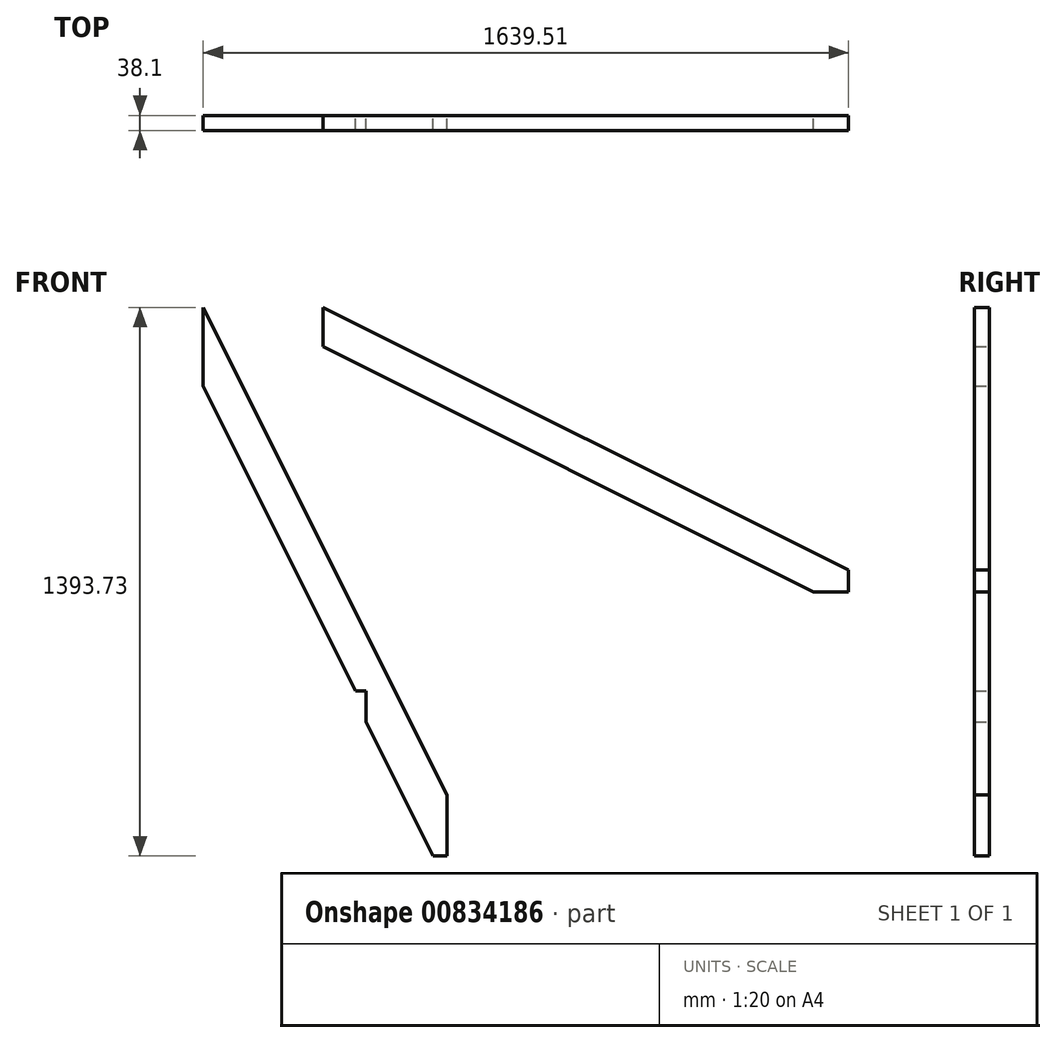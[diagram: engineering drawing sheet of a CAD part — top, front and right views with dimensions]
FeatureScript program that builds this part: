
annotation { "Feature Type Name" : "Feature", "Feature Type Description" : "" }
export const myFeature = defineFeature(function(context is Context, id is Id, definition is map)
    precondition{}
    {
        {
            var Q0;
            Q0=qCreatedBy(makeId("Front.planeOp"),FACE);
            var sketch = newSketch(context, id + "F0", { "sketchPlane" : qUnion([Q0])});
            skLineSegment(sketch, "E0", {"start": v(0, 0) * mm, "end": v(304.8, 0) * mm, "construction": true});
            skLineSegment(sketch, "E1", {"start": v(304.8, 0) * mm, "end": v(304.8, -609.6) * mm, "construction": true});
            skLineSegment(sketch, "E2", {"start": v(304.8, -609.6) * mm, "end": v(0, 0) * mm, "construction": true});
            skLineSegment(sketch, "E3", {"start": v(304.8, -609.6) * mm, "end": v(225.29, -649.36) * mm, "construction": true});
            skLineSegment(sketch, "E4", {"start": v(0, 0) * mm, "end": v(619.08, -1238.16) * mm});
            skLineSegment(sketch, "E5", {"start": v(619.08, -1238.16) * mm, "end": v(619.08, -1393.73) * mm});
            skLineSegment(sketch, "E6", {"start": v(619.08, -1393.73) * mm, "end": v(584.15, -1393.73) * mm});
            skLineSegment(sketch, "E7", {"start": v(584.15, -1393.73) * mm, "end": v(413.76, -1052.95) * mm});
            skLineSegment(sketch, "E8", {"start": v(413.76, -1052.95) * mm, "end": v(413.76, -973.58) * mm});
            skLineSegment(sketch, "E9", {"start": v(413.76, -973.58) * mm, "end": v(387.4, -973.58) * mm});
            skLineSegment(sketch, "E10", {"start": v(387.4, -973.58) * mm, "end": v(0, -198.79) * mm});
            skLineSegment(sketch, "E11", {"start": v(0, -198.79) * mm, "end": v(0, 0) * mm});
            skLineSegment(sketch, "E12", {"start": v(304.8, 0) * mm, "end": v(609.6, 0) * mm, "construction": true});
            skLineSegment(sketch, "E13", {"start": v(609.6, 0) * mm, "end": v(609.6, -152.4) * mm, "construction": true});
            skLineSegment(sketch, "E14", {"start": v(609.6, -152.4) * mm, "end": v(304.8, 0) * mm, "construction": true});
            skLineSegment(sketch, "E15", {"start": v(304.8, 0) * mm, "end": v(1639.5, -667.35) * mm});
            skLineSegment(sketch, "E16", {"start": v(1639.5, -667.35) * mm, "end": v(1639.5, -722.3) * mm});
            skLineSegment(sketch, "E17", {"start": v(1639.5, -722.3) * mm, "end": v(1550.6, -722.3) * mm});
            skLineSegment(sketch, "E18", {"start": v(1550.6, -722.3) * mm, "end": v(304.8, -99.4) * mm});
            skLineSegment(sketch, "E19", {"start": v(304.8, -99.4) * mm, "end": v(304.8, 0) * mm});
            skLineSegment(sketch, "E20", {"start": v(609.6, -152.4) * mm, "end": v(569.84, -231.91) * mm, "construction": true});
            skSolve(sketch);
        }
        {
            var Q0;
            Q0=makeQuery(id+"F0.imprint","IMPRINT",FACE,{"disambiguationData":[TD([[makeQuery(id+"F0.imprint","IMPRINT",EDGE,{"derivedFrom":sQuery(id+"F0.wireOp",EDGE,"E4")}),-1.0]])]});
            extrude(context, id + "F1", {"entities" : qUnion([Q0]), "depth" : 38.1 * mm, "offsetDistance" : 25.4 * mm});
        }
        {
            var Q0;
            Q0=makeQuery(id+"F0.imprint","IMPRINT",FACE,{"disambiguationData":[TD([[makeQuery(id+"F0.imprint","IMPRINT",EDGE,{"derivedFrom":sQuery(id+"F0.wireOp",EDGE,"E15")}),-1.0]])]});
            extrude(context, id + "F2", {"entities" : qUnion([Q0]), "depth" : 38.1 * mm, "offsetDistance" : 25.4 * mm});
        }
    });
